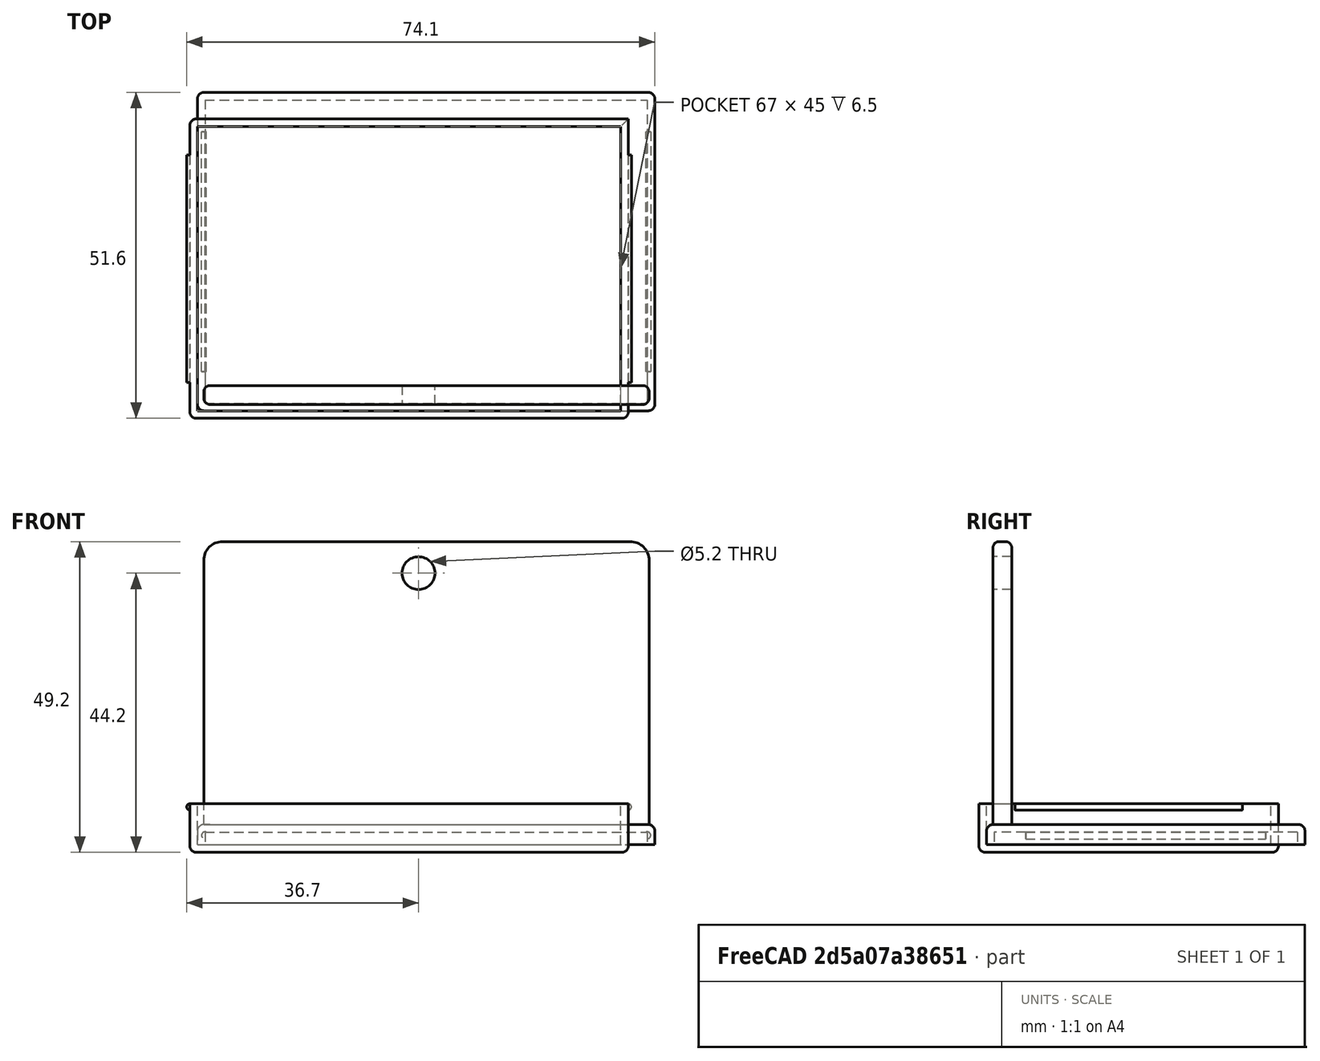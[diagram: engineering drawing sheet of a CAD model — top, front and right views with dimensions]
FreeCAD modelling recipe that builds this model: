
FCSTD DOCUMENT  (FreeCAD 0.21R33771 (Git))
Label: Growing_station_IR_LED_holdersimple_3d_print_box
License: Creative Commons Attribution-NonCommercial-ShareAlike 4.0
LicenseURL: http://creativecommons.org/licenses/by-nc-sa/4.0/
objects: Part::Box×5, Part::Cut×5, Part::Cylinder×5, Part::Fillet×4, Part::MultiFuse×2
note: 21 computed .brp shape members not serialized (recipe doc carries the construction recipe); baked Part::Feature solids carry a one-line shape summary decoded from their .brp

FEATURE [Part::Box] case_inside
  AttacherType = Attacher::AttachEngine3D
  Height = 6.5
  Length = 67
  Width = 45
FEATURE [Part::Box] case_outside
  AttacherType = Attacher::AttachEngine3D
  Height = 7.7
  Length = 69.4
  Placement = pos=(-1.2,-1.2,-1.2) rot=(0,0,1;0rad)
  Width = 47.4
FEATURE [Part::Cut] Cut  label="case_cut_inside_outside"
  Base = -> case_outside
  Tool = -> case_inside
FEATURE [Part::Cylinder] tongue_left
  Angle = 360
  AttacherType = Attacher::AttachEngine3D
  FirstAngle = 0
  Height = 36
  Placement = pos=(-1.2,4.5,6) rot=(1,0,0;-1.5708rad)
  Radius = 0.5
  SecondAngle = 0
FEATURE [Part::Cylinder] lid_groove_left
  Angle = 360
  AttacherType = Attacher::AttachEngine3D
  FirstAngle = 0
  Height = 38
  Placement = pos=(-1.5,3.5,0.5) rot=(1,0,0;-1.5708rad)
  Radius = 0.55
  SecondAngle = 0
FEATURE [Part::Cylinder] tongue_right
  Angle = 360
  AttacherType = Attacher::AttachEngine3D
  FirstAngle = 0
  Height = 36
  Placement = pos=(68.2,4.5,6) rot=(1,0,0;-1.5708rad)
  Radius = 0.5
  SecondAngle = 0
FEATURE [Part::Cylinder] lid_groove_right
  Angle = 360
  AttacherType = Attacher::AttachEngine3D
  FirstAngle = 0
  Height = 38
  Placement = pos=(68.5,3.5,0.5) rot=(1,0,0;-1.5708rad)
  Radius = 0.55
  SecondAngle = 0
FEATURE [Part::MultiFuse] Fusion  label="fusion_case_tongues"
  Shapes = -> [Cut,tongue_left,tongue_right]
FEATURE [Part::Fillet] Fillet  label="case"
  Base = -> Fusion
  Edges = 7 edges r=1: [Edge18,Edge19,Edge20,Edge21,Edge23,Edge24,Edge28]
FEATURE [Part::Box] lid_inside
  AttacherType = Attacher::AttachEngine3D
  Height = 2
  Length = 70
  Placement = pos=(-1.5,-1.5,0) rot=(0,0,1;0rad)
  Width = 48
FEATURE [Part::Box] lid_outside
  AttacherType = Attacher::AttachEngine3D
  Height = 3.2
  Length = 72.4
  Placement = pos=(-2.7,-2.7,-1.2) rot=(0,0,1;0rad)
  Width = 50.4
FEATURE [Part::Cut] Cut001  label="lid_cut_inside_outside"
  Base = -> lid_outside
  Tool = -> lid_inside
FEATURE [Part::Cut] Cut002  label="lid_cut_groove"
  Base = -> Cut001
  Tool = -> lid_groove_right
FEATURE [Part::Cut] Cut003  label="lid_cut_groove_left"
  Base = -> Cut002
  Tool = -> lid_groove_left
FEATURE [Part::Fillet] Fillet001  label="lid"
  Base = -> Cut003
  Edges = 8 edges r=1: [Edge1,Edge3,Edge4,Edge5,Edge6,Edge14,Edge15,Edge16]
  Placement = pos=(2.7,47.7,2) rot=(1,0,0;3.14159rad)
FEATURE [Part::Box] Box  label="Cube"
  AttacherType = Attacher::AttachEngine3D
  Height = 45
  Length = 70.5
  Placement = pos=(1,1,3) rot=(0,0,1;0rad)
  Width = 3
FEATURE [Part::Cylinder] Cylinder
  Angle = 360
  AttacherType = Attacher::AttachEngine3D
  FirstAngle = 0
  Height = 10
  Placement = pos=(35,9.5e-15,43) rot=(1,0,0;4.71239rad)
  Radius = 2.6
  SecondAngle = 0
FEATURE [Part::Cut] Cut004
  Base = -> Box
  Tool = -> Cylinder
FEATURE [Part::Fillet] Fillet002
  Base = -> Cut004
  Edges = 2 edges r=3: [Edge2,Edge10]
FEATURE [Part::Fillet] Fillet003  label="fillet"
  Base = -> Fillet002
  Edges = 4 edges r=1: [Edge1,Edge3,Edge8,Edge16]
FEATURE [Part::MultiFuse] Fusion001  label="lid_with_led_holder"
  Shapes = -> [Fillet001,Fillet003]
